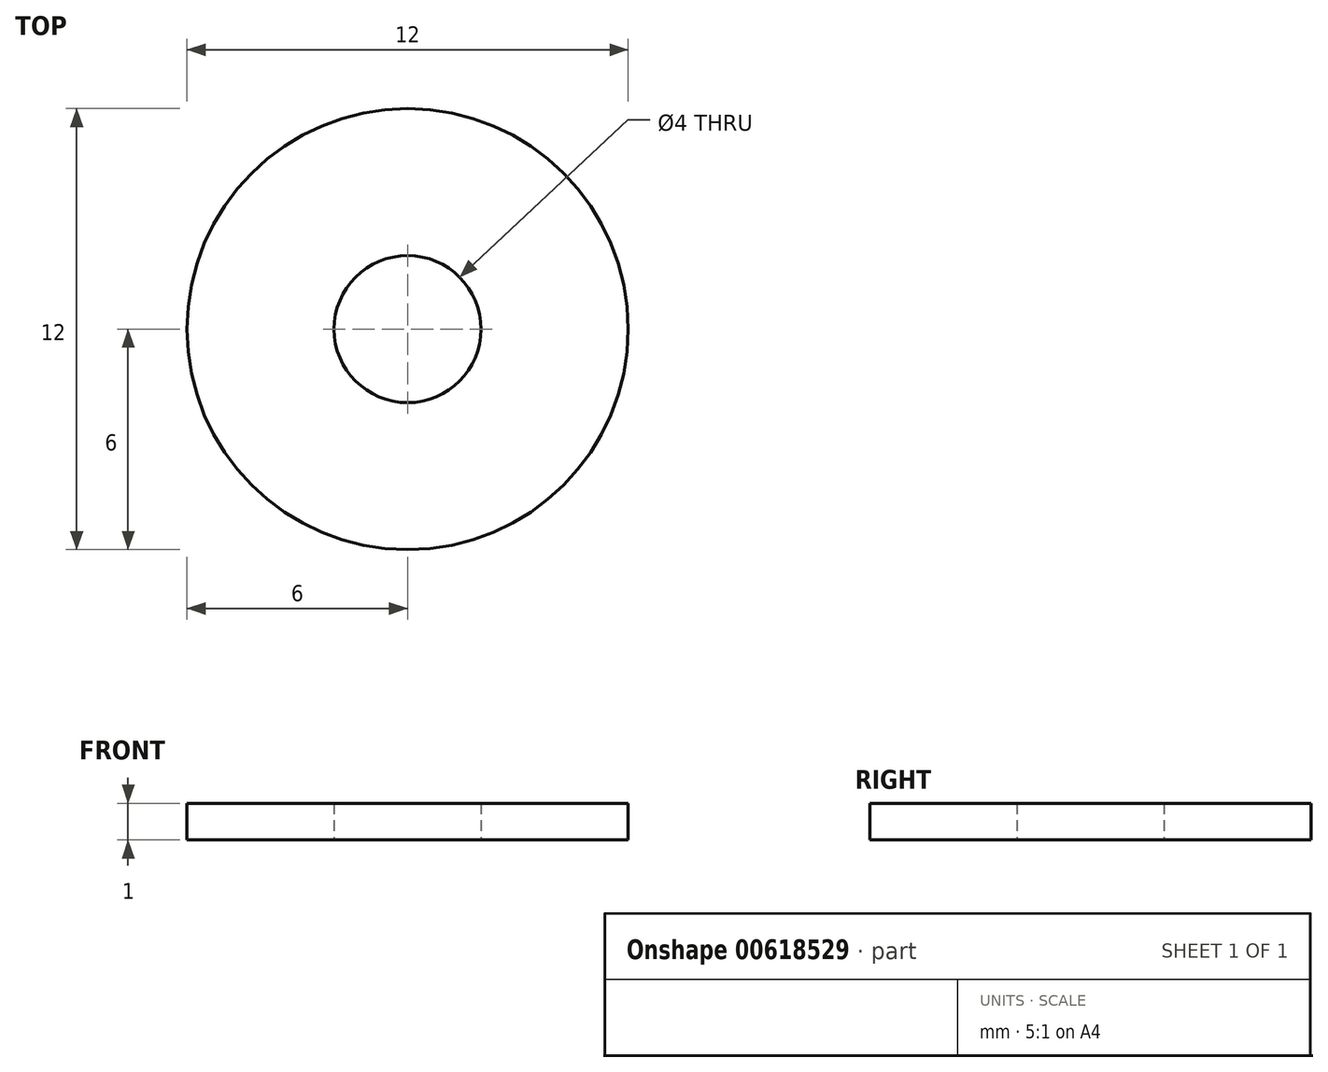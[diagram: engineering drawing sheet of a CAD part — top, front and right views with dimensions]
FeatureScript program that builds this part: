
annotation { "Feature Type Name" : "Feature", "Feature Type Description" : "" }
export const myFeature = defineFeature(function(context is Context, id is Id, definition is map)
    precondition{}
    {
        {
            var Q0;
            Q0=qCreatedBy(makeId("Top.planeOp"),FACE);
            var sketch = newSketch(context, id + "F0", { "sketchPlane" : qUnion([Q0])});
            skCircle(sketch, "E0", {"center": v(0, 0) * mm, "radius": 2 * mm});
            skCircle(sketch, "E1", {"center": v(0, 0) * mm, "radius": 6 * mm});
            skSolve(sketch);
        }
        {
            var Q0;
            Q0=makeQuery(id+"F0.imprint","IMPRINT",FACE,{"disambiguationData":[TD([[makeQuery(id+"F0.imprint","IMPRINT",EDGE,{"derivedFrom":sQuery(id+"F0.wireOp",EDGE,"E0")}),-1.0]])]});
            extrude(context, id + "F1", {"entities" : qUnion([Q0]), "depth" : 1 * mm, "offsetDistance" : 25 * mm});
        }
    });
